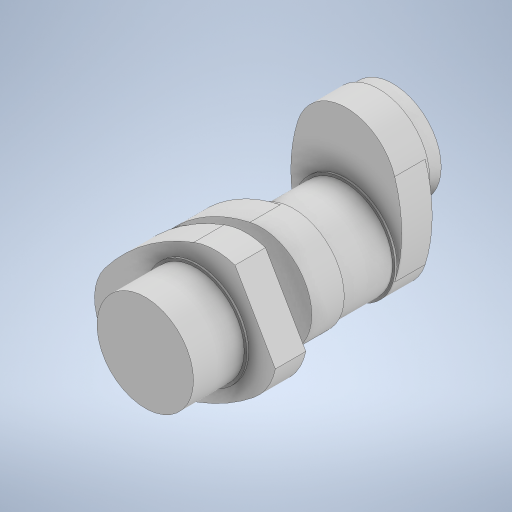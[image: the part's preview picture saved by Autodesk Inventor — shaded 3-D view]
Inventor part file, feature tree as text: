
AUTODESK INVENTOR PART (.ipt)
format: ipt  version: 2024 (Build 280153020, 153B)  size: 382,976 bytes
history: native  units: mm
features: extrude x13, sketch x13, projected_geometry x1
ambient origin geometry x8: Origin, YZ Plane, XZ Plane, XY Plane, X Axis, Y Axis, Z Axis, Center Point
bodies: Body1 (feature_tree)
feature tree (27):
  extrude  "Extrusion6"  Depth=95.0mm
  extrude  "Extrusion7"  Depth=100.0mm
  extrude  "Extrusion8"  Depth=100.0mm
  extrude  "Extrusion13"  Depth=100.0mm
  extrude  "Extrusion14"  Depth=30.0mm TaperAngle=0.0deg
  extrude  "Extrusion20"  Depth=60.0mm
  extrude  "Extrusion21"  Depth=2.0mm TaperAngle=0.0deg
  extrude  "Extrusion29"  Depth=50.0mm TaperAngle=0.0deg
  extrude  "Extrusion30"  Depth=2.0mm TaperAngle=0.0deg
  extrude  "Extrusion31"  Depth=60.0mm
  extrude  "Extrusion32"  Depth=30.0mm TaperAngle=0.0deg
  extrude  "Extrusion33"  Depth=100.0mm
  extrude  "Extrusion34"  Depth=50.0mm
  sketch  "Sketch8"  dims[d20=120.0mm d28=95.0mm]
  sketch  "Sketch9"  dims[d29=14.0mm d30=0.0mm d31=100.0mm]
  sketch  "Sketch10"  dims[d32=2.0mm d33=0.0mm d34=100.0mm]
  sketch  "Sketch15"  dims[d35=60.0mm d37=100.0mm]
  projected_geometry  "Projected Loop1"
  sketch  "Sketch16"  dims[d38=150.0mm d39=30.0mm d40=0.0mm]
  sketch  "Sketch22"  dims[d44=120.0mm d61=60.0mm]
  sketch  "Sketch23"  dims[d62=100.0mm d63=2.0mm d64=0.0mm]
  sketch  "Sketch31"  dims[d65=95.0mm d66=50.0mm d67=0.0mm]
  sketch  "Sketch32"  dims[d92=100.0mm d93=2.0mm d94=0.0mm]
  sketch  "Sketch33"  dims[d95=120.0deg d96=60.0mm]
  sketch  "Sketch34"  dims[d101=150.0mm d102=30.0mm d103=0.0mm]
  sketch  "Sketch35"  dims[d119=120.0mm d129=100.0mm d131=120.0mm d144=100.0mm]
  sketch  "Sketch36"  dims[d145=2.0mm d146=0.0mm d147=95.0mm d148=28.0mm d149=0.0mm d150=100.0mm d151=2.0mm d152=0.0mm d153=30.0deg d155=80.0mm d156=120.0mm d158=125.0mm d159=60.0mm d160=200.0mm d161=30.0mm d162=0.0mm d163=100.0mm d164=2.0mm d165=0.0mm d166=95.0mm d167=50.0mm d168=0.0mm d59=0.5mm d60=0.872665mm]
